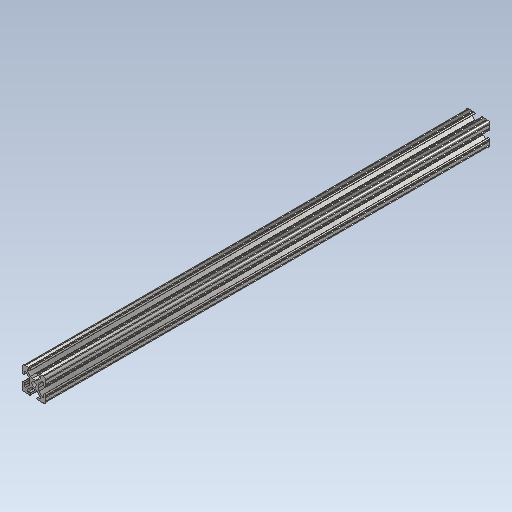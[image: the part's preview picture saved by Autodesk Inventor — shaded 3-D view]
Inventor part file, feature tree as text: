
AUTODESK INVENTOR PART (.ipt)
format: ipt  version: 2020 (Build 240168000, 168)  size: 243,200 bytes
history: native  units: in
note: dims shown in document units (in); Inventor stores cm internally (conversion verified against a paired STEP export)
features: extrude x1, sketch x1
ambient origin geometry x8: Origin, YZ Plane, XZ Plane, XY Plane, X Axis, Y Axis, Z Axis, Center Point
bodies: Solid1 (feature_tree)
feature tree (2):
  extrude  "Extrusion1"  [1 undecoded]
  sketch  "Sketch1"  dims[d0=19.0in d1=0.0in]
note: 1 required parameter value undecoded (feature->parameter linkage not recoverable at this tier; creation-order binding heuristic only, values carry confidence <= 0.55)
